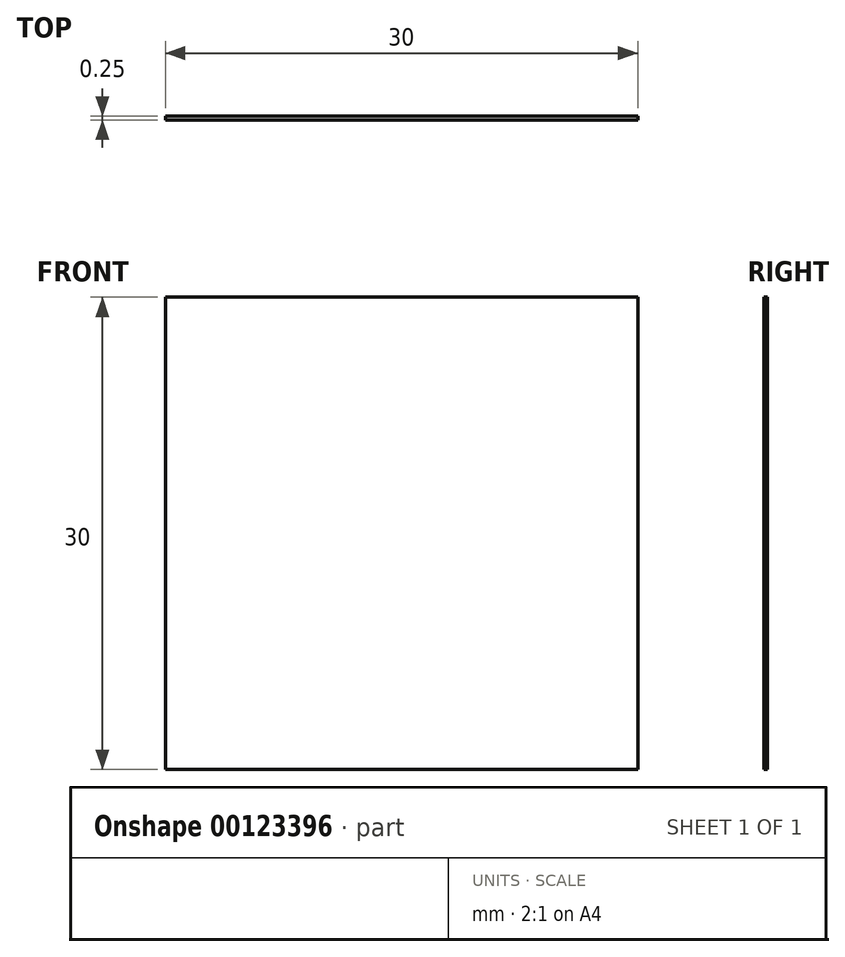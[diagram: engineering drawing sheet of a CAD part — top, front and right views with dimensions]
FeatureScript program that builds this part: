
annotation { "Feature Type Name" : "Feature", "Feature Type Description" : "" }
export const myFeature = defineFeature(function(context is Context, id is Id, definition is map)
    precondition{}
    {
        {
            var Q0;
            Q0=qCreatedBy(makeId("Front.planeOp"),FACE);
            var sketch = newSketch(context, id + "F0", { "sketchPlane" : qUnion([Q0])});
            skLineSegment(sketch, "E0.bottom", {"start": v(0, 0) * mm, "end": v(-30, 0) * mm});
            skLineSegment(sketch, "E0.top", {"start": v(0, 30) * mm, "end": v(-30, 30) * mm});
            skLineSegment(sketch, "E0.left", {"start": v(0, 0) * mm, "end": v(0, 30) * mm});
            skLineSegment(sketch, "E0.right", {"start": v(-30, 0) * mm, "end": v(-30, 30) * mm});
            skSolve(sketch);
        }
        {
            var Q0;
            Q0=makeQuery(id+"F0.imprint","IMPRINT",FACE,{"disambiguationData":[TD([[makeQuery(id+"F0.imprint","IMPRINT",EDGE,{"derivedFrom":sQuery(id+"F0.wireOp",EDGE,"E0.bottom")}),-1.0]])]});
            extrude(context, id + "F1", {"entities" : qUnion([Q0]), "depth" : 0.25 * mm});
        }
    });
